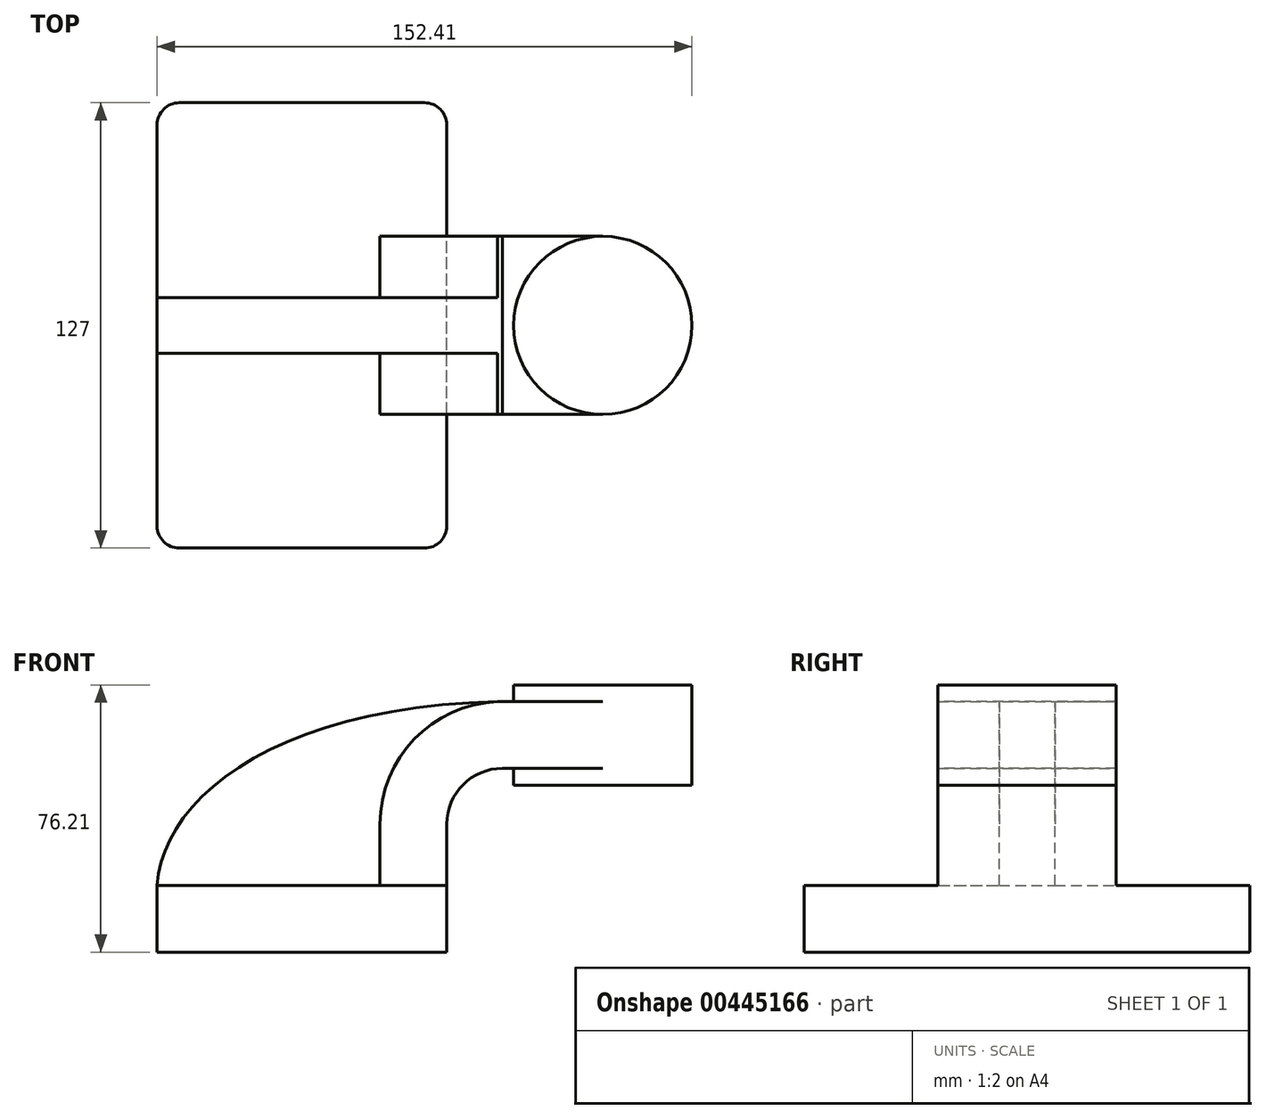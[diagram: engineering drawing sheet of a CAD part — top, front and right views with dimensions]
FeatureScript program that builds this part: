
annotation { "Feature Type Name" : "Feature", "Feature Type Description" : "" }
export const myFeature = defineFeature(function(context is Context, id is Id, definition is map)
    precondition{}
    {
        {
            var Q0;
            Q0=qCreatedBy(makeId("Front.planeOp"),FACE);
            var sketch = newSketch(context, id + "F0", { "sketchPlane" : qUnion([Q0])});
            skLineSegment(sketch, "E0.bottom", {"start": v(-41.28, -9.53) * mm, "end": v(41.28, -9.53) * mm});
            skLineSegment(sketch, "E0.top", {"start": v(-41.28, 9.52) * mm, "end": v(41.28, 9.52) * mm});
            skLineSegment(sketch, "E0.left", {"start": v(-41.28, -9.53) * mm, "end": v(-41.28, 9.52) * mm});
            skLineSegment(sketch, "E0.right", {"start": v(41.28, -9.53) * mm, "end": v(41.28, 9.52) * mm});
            skPoint(sketch, "E0.middle", {"position": v(0, 0) * mm});
            skLineSegment(sketch, "E1.bottom", {"start": v(60.32, 38.1) * mm, "end": v(111.12, 38.1) * mm});
            skLineSegment(sketch, "E1.top", {"start": v(60.32, 66.67) * mm, "end": v(111.12, 66.67) * mm});
            skLineSegment(sketch, "E1.left", {"start": v(60.32, 38.1) * mm, "end": v(60.32, 66.67) * mm});
            skLineSegment(sketch, "E1.right", {"start": v(111.12, 38.1) * mm, "end": v(111.12, 66.67) * mm});
            skPoint(sketch, "E1.middle", {"position": v(85.72, 52.39) * mm});
            skLineSegment(sketch, "E2", {"start": v(41.28, 9.52) * mm, "end": v(41.28, 27) * mm});
            skArc(sketch, "E3", {"start": v(41.27, 27) * mm, "mid": v(45.92, 38.23) * mm, "end": v(57.15, 42.88) * mm});
            skLineSegment(sketch, "E4", {"start": v(57.15, 42.88) * mm, "end": v(85.72, 42.88) * mm});
            skLineSegment(sketch, "E5.0", {"start": v(57.15, 61.93) * mm, "end": v(85.72, 61.93) * mm});
            skArc(sketch, "E5.1", {"start": v(22.22, 27) * mm, "mid": v(32.45, 51.7) * mm, "end": v(57.15, 61.93) * mm});
            skLineSegment(sketch, "E5.2", {"start": v(22.23, 9.52) * mm, "end": v(22.23, 27) * mm});
            skLineSegment(sketch, "E6", {"start": v(85.72, 66.67) * mm, "end": v(85.72, 38.1) * mm});
            skFitSpline(sketch, "E7", {"points": [v(-41.28, 9.53) * mm, v(57.15, 61.93) * mm], "startDerivative": vector(5.04, 75.1) * mm, "endDerivative": vector(192.93, 3.33) * mm});
            skSolve(sketch);
        }
        {
            var Q0;
            Q0=makeQuery(id+"F0.imprint","IMPRINT",FACE,{"disambiguationData":[TD([[makeQuery(id+"F0.imprint","IMPRINT",EDGE,{"derivedFrom":sQuery(id+"F0.wireOp",EDGE,"E0.bottom")}),1.0]])]});
            extrude(context, id + "F1", {"entities" : qUnion([Q0]), "depth" : 127 * mm, "symmetric" : true});
        }
        {
            var Q0;
            {var subQ3=sQuery(id+"F0.wireOp",EDGE,"E5.2");Q0=makeQuery(id+"F0.imprint","IMPRINT",FACE,{"disambiguationData":[TD([[makeQuery(id+"F0.imprint","IMPRINT",EDGE,{"derivedFrom":subQ3}),1.0]])]});}
            extrude(context, id + "F2", {"entities" : qUnion([Q0]), "operationType" : NewBodyOperationType.ADD, "depth" : 15.88 * mm, "symmetric" : true});
        }
        {
            var Q0;
            {var subQ1=sQuery(id+"F0.wireOp",EDGE,"E2");Q0=makeQuery(id+"F0.imprint","IMPRINT",FACE,{"disambiguationData":[TD([[makeQuery(id+"F0.imprint","IMPRINT",EDGE,{"derivedFrom":subQ1}),1.0]])]});}
            var Q1;
            {var subQ0=sQuery(id+"F0.wireOp",EDGE,"E4");var subQ1=sQuery(id+"F0.wireOp",EDGE,"E1.left");var subQ2=makeQuery(id+"F0.imprint","INTERSECT",VERTEX,{"derivedFrom":[subQ1,subQ0]});Q1=makeQuery(id+"F0.imprint","IMPRINT",FACE,{"disambiguationData":[TD([[makeQuery(id+"F0.imprint","IMPRINT",EDGE,{"disambiguationData":[TD([[subQ2,-1.0]])],"derivedFrom":subQ1}),-1.0]])]});}
            extrude(context, id + "F3", {"entities" : qUnion([Q0, Q1]), "operationType" : NewBodyOperationType.ADD, "depth" : 50.8 * mm, "symmetric" : true});
        }
        {
            var Q0;
            {var subQ4=sQuery(id+"F0.wireOp",EDGE,"E1.right");Q0=makeQuery(id+"F0.imprint","IMPRINT",FACE,{"disambiguationData":[TD([[makeQuery(id+"F0.imprint","IMPRINT",EDGE,{"derivedFrom":subQ4}),1.0]])]});}
            var Q1;
            Q1=sQuery(id+"F0.wireOp",EDGE,"E6");
            revolve(context, id + "F4", {"operationType" : NewBodyOperationType.ADD, "entities" : qUnion([Q0]), "axis" : qUnion([Q1]), "revolveType" : RevolveType.FULL});
        }
        {
            var Q0;
            Q0=makeQuery(id+"F1.opExtrude","CAP_EDGE",EDGE,{"disambiguationData":[OSD([sQuery(id+"F0.wireOp",EDGE,"E0.right")])],"isStart":false});
            var Q1;
            Q1=makeQuery(id+"F1.opExtrude","CAP_EDGE",EDGE,{"disambiguationData":[OSD([sQuery(id+"F0.wireOp",EDGE,"E0.left")])],"isStart":false});
            var Q2;
            Q2=makeQuery(id+"F1.opExtrude","CAP_EDGE",EDGE,{"disambiguationData":[OSD([sQuery(id+"F0.wireOp",EDGE,"E0.right")])],"isStart":true});
            var Q3;
            Q3=makeQuery(id+"F1.opExtrude","CAP_EDGE",EDGE,{"disambiguationData":[OSD([sQuery(id+"F0.wireOp",EDGE,"E0.left")])],"isStart":true});
            fillet(context, id + "F5", {"entities" : qUnion([Q0, Q1, Q2, Q3]), "radius" : 6.35 * mm, "tangentPropagation" : true, "allowEdgeOverflow" : false});
        }
    });
